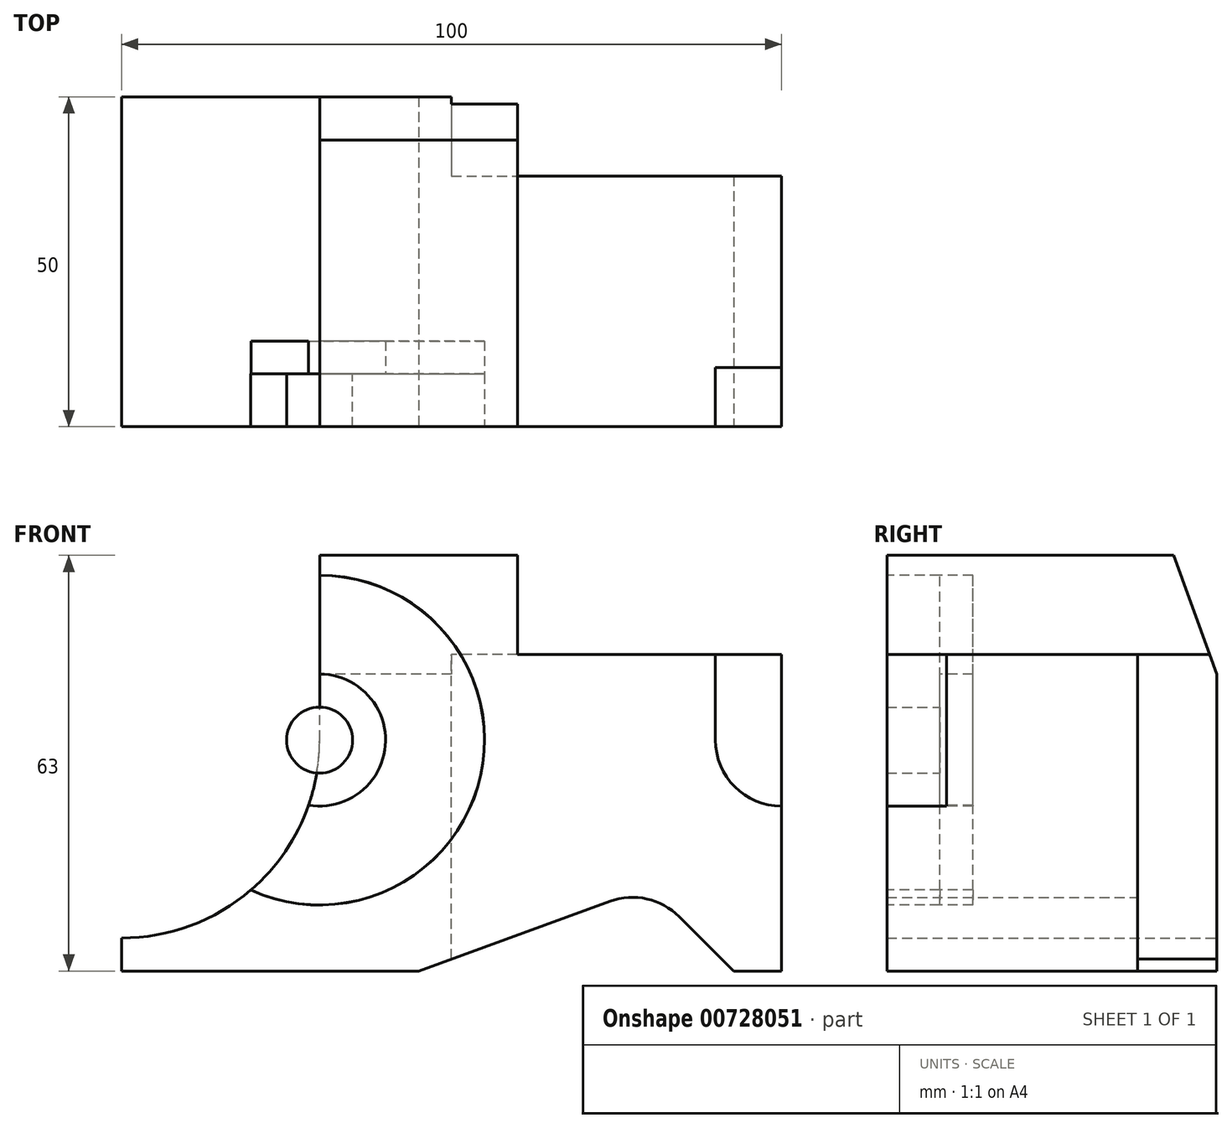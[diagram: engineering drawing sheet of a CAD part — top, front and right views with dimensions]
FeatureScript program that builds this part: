
annotation { "Feature Type Name" : "Feature", "Feature Type Description" : "" }
export const myFeature = defineFeature(function(context is Context, id is Id, definition is map)
    precondition{}
    {
        {
            var Q0;
            Q0=qCreatedBy(makeId("Front.planeOp"),FACE);
            var sketch = newSketch(context, id + "F0", { "sketchPlane" : qUnion([Q0])});
            skLineSegment(sketch, "E0.bottom", {"start": v(0, 0) * mm, "end": v(100, 0) * mm});
            skLineSegment(sketch, "E0.top", {"start": v(0, 63) * mm, "end": v(100, 63) * mm});
            skLineSegment(sketch, "E0.left", {"start": v(0, 0) * mm, "end": v(0, 63) * mm});
            skLineSegment(sketch, "E0.right", {"start": v(100, 0) * mm, "end": v(100, 63) * mm});
            skSolve(sketch);
        }
        {
            var Q0;
            Q0=makeQuery(id+"F0.imprint","IMPRINT",FACE,{"disambiguationData":[TD([[makeQuery(id+"F0.imprint","IMPRINT",EDGE,{"derivedFrom":sQuery(id+"F0.wireOp",EDGE,"E0.bottom")}),1.0]])]});
            extrude(context, id + "F1", {"entities" : qUnion([Q0]), "depth" : 50 * mm, "offsetDistance" : 25.4 * mm});
        }
        {
            var Q0;
            Q0=makeQuery(id+"F1.opExtrude","CAP_FACE",FACE,{"disambiguationData":[OSD([sQuery(id+"F0.wireOp",EDGE,"E0.bottom"),sQuery(id+"F0.wireOp",EDGE,"E0.top"),sQuery(id+"F0.wireOp",EDGE,"E0.left"),sQuery(id+"F0.wireOp",EDGE,"E0.right")])],"isStart":false});
            var sketch = newSketch(context, id + "F2", { "sketchPlane" : qUnion([Q0])});
            skLineSegment(sketch, "E1.bottom", {"start": v(100, 63) * mm, "end": v(60, 63) * mm});
            skLineSegment(sketch, "E1.top", {"start": v(100, 48) * mm, "end": v(60, 48) * mm});
            skLineSegment(sketch, "E1.left", {"start": v(100, 63) * mm, "end": v(100, 48) * mm});
            skLineSegment(sketch, "E1.right", {"start": v(60, 63) * mm, "end": v(60, 48) * mm});
            skLineSegment(sketch, "E2", {"start": v(45, 0) * mm, "end": v(80, 12.74) * mm});
            skPoint(sketch, "E2.endSnap0", {"position": v(80, 48) * mm});
            skLineSegment(sketch, "E3", {"start": v(80, 12.74) * mm, "end": v(92.74, 0) * mm});
            skLineSegment(sketch, "E4", {"start": v(92.74, 0) * mm, "end": v(45, 0) * mm});
            skSolve(sketch);
        }
        {
            var Q0;
            Q0 = qSketchRegion(id + "F2", true);
            extrude(context, id + "F3", {"entities" : qUnion([Q0]), "operationType" : NewBodyOperationType.REMOVE, "endBound" : BoundingType.UP_TO_NEXT, "oppositeDirection" : true, "depth" : 50 * mm, "offsetDistance" : 25.4 * mm});
        }
        {
            var Q0;
            Q0=makeQuery(id+"F1.opExtrude","CAP_FACE",FACE,{"disambiguationData":[OSD([sQuery(id+"F0.wireOp",EDGE,"E0.bottom"),sQuery(id+"F0.wireOp",EDGE,"E0.top"),sQuery(id+"F0.wireOp",EDGE,"E0.left"),sQuery(id+"F0.wireOp",EDGE,"E0.right")])],"isStart":false});
            var sketch = newSketch(context, id + "F4", { "sketchPlane" : qUnion([Q0])});
            skLineSegment(sketch, "E5.bottom", {"start": v(100, 48) * mm, "end": v(90, 48) * mm});
            skLineSegment(sketch, "E5.right", {"start": v(90, 48) * mm, "end": v(90, 35) * mm});
            skArc(sketch, "E6", {"start": v(90, 35) * mm, "mid": v(92.93, 27.93) * mm, "end": v(100, 25) * mm});
            skLineSegment(sketch, "E7", {"start": v(100, 48) * mm, "end": v(100, 25) * mm});
            skSolve(sketch);
        }
        {
            var Q0;
            Q0 = qSketchRegion(id + "F4", true);
            extrude(context, id + "F5", {"entities" : qUnion([Q0]), "operationType" : NewBodyOperationType.REMOVE, "oppositeDirection" : true, "depth" : 9 * mm, "offsetDistance" : 25.4 * mm});
        }
        {
            var Q0;
            Q0=makeQuery(id+"F3.boolean.opBoolean","COPY",EDGE,{"derivedFrom":makeQuery(id+"F3.opExtrude","SWEPT_EDGE",EDGE,{"disambiguationData":[OSD([sQuery(id+"F2.wireOp",EDGE,"E2"),sQuery(id+"F2.wireOp",EDGE,"E3")])]})});
            fillet(context, id + "F6", {"entities" : qUnion([Q0]), "radius" : 10 * mm, "tangentPropagation" : true, "allowEdgeOverflow" : false});
        }
        {
            var Q0;
            Q0=makeQuery(id+"F3.boolean.opBoolean","COPY",FACE,{"derivedFrom":makeQuery(id+"F3.opExtrude","SWEPT_FACE",FACE,{"disambiguationData":[OSD([sQuery(id+"F2.wireOp",EDGE,"E1.top")])]})});
            var sketch = newSketch(context, id + "F7", { "sketchPlane" : qUnion([Q0])});
            skLineSegment(sketch, "E8.bottom", {"start": v(50, 0) * mm, "end": v(100, 0) * mm});
            skLineSegment(sketch, "E8.top", {"start": v(50, -12) * mm, "end": v(100, -12) * mm});
            skLineSegment(sketch, "E8.left", {"start": v(50, 0) * mm, "end": v(50, -12) * mm});
            skLineSegment(sketch, "E8.right", {"start": v(100, 0) * mm, "end": v(100, -12) * mm});
            skSolve(sketch);
        }
        {
            var Q0;
            Q0 = qSketchRegion(id + "F7", true);
            extrude(context, id + "F8", {"entities" : qUnion([Q0]), "operationType" : NewBodyOperationType.REMOVE, "endBound" : BoundingType.UP_TO_NEXT, "oppositeDirection" : true, "depth" : 25.4 * mm, "offsetDistance" : 25.4 * mm});
        }
        {
            var Q0;
            Q0=makeQuery(id+"F1.opExtrude","CAP_FACE",FACE,{"disambiguationData":[OSD([sQuery(id+"F0.wireOp",EDGE,"E0.bottom"),sQuery(id+"F0.wireOp",EDGE,"E0.top"),sQuery(id+"F0.wireOp",EDGE,"E0.left"),sQuery(id+"F0.wireOp",EDGE,"E0.right")])],"isStart":true});
            var sketch = newSketch(context, id + "F9", { "sketchPlane" : qUnion([Q0])});
            skArc(sketch, "E9", {"start": v(-30, 35) * mm, "mid": v(-21.21, 13.79) * mm, "end": v(0, 5) * mm});
            skLineSegment(sketch, "E10", {"start": v(-30, 35) * mm, "end": v(-30, 63) * mm});
            skLineSegment(sketch, "E11", {"start": v(-30, 63) * mm, "end": v(0, 63) * mm});
            skLineSegment(sketch, "E12", {"start": v(0, 63) * mm, "end": v(0, 5) * mm});
            skSolve(sketch);
        }
        {
            var Q0;
            Q0 = qSketchRegion(id + "F9", true);
            extrude(context, id + "F10", {"entities" : qUnion([Q0]), "operationType" : NewBodyOperationType.REMOVE, "endBound" : BoundingType.UP_TO_NEXT, "oppositeDirection" : true, "depth" : 25.4 * mm, "offsetDistance" : 25.4 * mm});
        }
        {
            var Q0;
            Q0=makeQuery(id+"F1.opExtrude","CAP_FACE",FACE,{"disambiguationData":[OSD([sQuery(id+"F0.wireOp",EDGE,"E0.bottom"),sQuery(id+"F0.wireOp",EDGE,"E0.top"),sQuery(id+"F0.wireOp",EDGE,"E0.left"),sQuery(id+"F0.wireOp",EDGE,"E0.right")])],"isStart":false});
            var sketch = newSketch(context, id + "F11", { "sketchPlane" : qUnion([Q0])});
            skCircle(sketch, "E13", {"center": v(30, 35) * mm, "radius": 25 * mm});
            skSolve(sketch);
        }
        {
            var Q0;
            Q0 = qSketchRegion(id + "F11", true);
            extrude(context, id + "F12", {"entities" : qUnion([Q0]), "operationType" : NewBodyOperationType.REMOVE, "oppositeDirection" : true, "depth" : 8 * mm, "offsetDistance" : 25.4 * mm});
        }
        {
            var Q0;
            Q0=makeQuery(id+"F12.boolean.opBoolean","COPY",FACE,{"derivedFrom":makeQuery(id+"F12.opExtrude","CAP_FACE",FACE,{"disambiguationData":[OSD([sQuery(id+"F11.wireOp",EDGE,"E13")])],"isStart":false})});
            var sketch = newSketch(context, id + "F13", { "sketchPlane" : qUnion([Q0])});
            skPoint(sketch, "E14", {"position": v(30, 35) * mm});
            skCircle(sketch, "E15", {"center": v(30, 35) * mm, "radius": 10 * mm});
            skCircle(sketch, "E16", {"center": v(30, 35) * mm, "radius": 24.98 * mm});
            skSolve(sketch);
        }
        {
            var Q0;
            Q0 = qSketchRegion(id + "F13", true);
            extrude(context, id + "F14", {"entities" : qUnion([Q0]), "operationType" : NewBodyOperationType.REMOVE, "oppositeDirection" : true, "depth" : 5 * mm, "offsetDistance" : 25.4 * mm});
        }
        {
            var Q0;
            Q0=makeQuery(id+"F14.boolean.opBoolean","SPLIT",FACE,{"disambiguationData":[TD([makeQuery(id+"F14.opExtrude","SWEPT_FACE",FACE,{"disambiguationData":[OSD([sQuery(id+"F13.wireOp",EDGE,"E15")])]})])],"derivedFrom":makeQuery(id+"F12.boolean.opBoolean","COPY",FACE,{"derivedFrom":makeQuery(id+"F12.opExtrude","CAP_FACE",FACE,{"disambiguationData":[OSD([sQuery(id+"F11.wireOp",EDGE,"E13")])],"isStart":false})})});
            var sketch = newSketch(context, id + "F15", { "sketchPlane" : qUnion([Q0])});
            skPoint(sketch, "E17", {"position": v(30, 35) * mm});
            skCircle(sketch, "E18", {"center": v(30, 35) * mm, "radius": 5 * mm});
            skSolve(sketch);
        }
        {
            var Q0;
            Q0 = qSketchRegion(id + "F15", true);
            var Q1;
            Q1=makeQuery(id+"F1.opExtrude","CAP_FACE",FACE,{"disambiguationData":[OSD([sQuery(id+"F0.wireOp",EDGE,"E0.bottom"),sQuery(id+"F0.wireOp",EDGE,"E0.top"),sQuery(id+"F0.wireOp",EDGE,"E0.left"),sQuery(id+"F0.wireOp",EDGE,"E0.right")])],"isStart":false});
            extrude(context, id + "F16", {"entities" : qUnion([Q0]), "operationType" : NewBodyOperationType.ADD, "endBound" : BoundingType.UP_TO_SURFACE, "depth" : 25.4 * mm, "endBoundEntityFace" : qUnion([Q1]), "offsetDistance" : 25.4 * mm});
        }
        {
            var Q0;
            Q0=makeQuery(id+"F10.boolean.opBoolean","COPY",FACE,{"derivedFrom":makeQuery(id+"F10.opExtrude","SWEPT_FACE",FACE,{"disambiguationData":[OSD([sQuery(id+"F9.wireOp",EDGE,"E10")])]})});
            var sketch = newSketch(context, id + "F17", { "sketchPlane" : qUnion([Q0])});
            skLineSegment(sketch, "E19", {"start": v(0, 63) * mm, "end": v(6.55, 63) * mm});
            skLineSegment(sketch, "E20", {"start": v(6.55, 63) * mm, "end": v(0, 45) * mm});
            skLineSegment(sketch, "E21", {"start": v(0, 45) * mm, "end": v(0, 63) * mm});
            skSolve(sketch);
        }
        {
            var Q0;
            Q0 = qSketchRegion(id + "F17", true);
            extrude(context, id + "F18", {"entities" : qUnion([Q0]), "operationType" : NewBodyOperationType.REMOVE, "endBound" : BoundingType.THROUGH_ALL, "oppositeDirection" : true, "depth" : 25.4 * mm, "offsetDistance" : 25.4 * mm});
        }
    });
